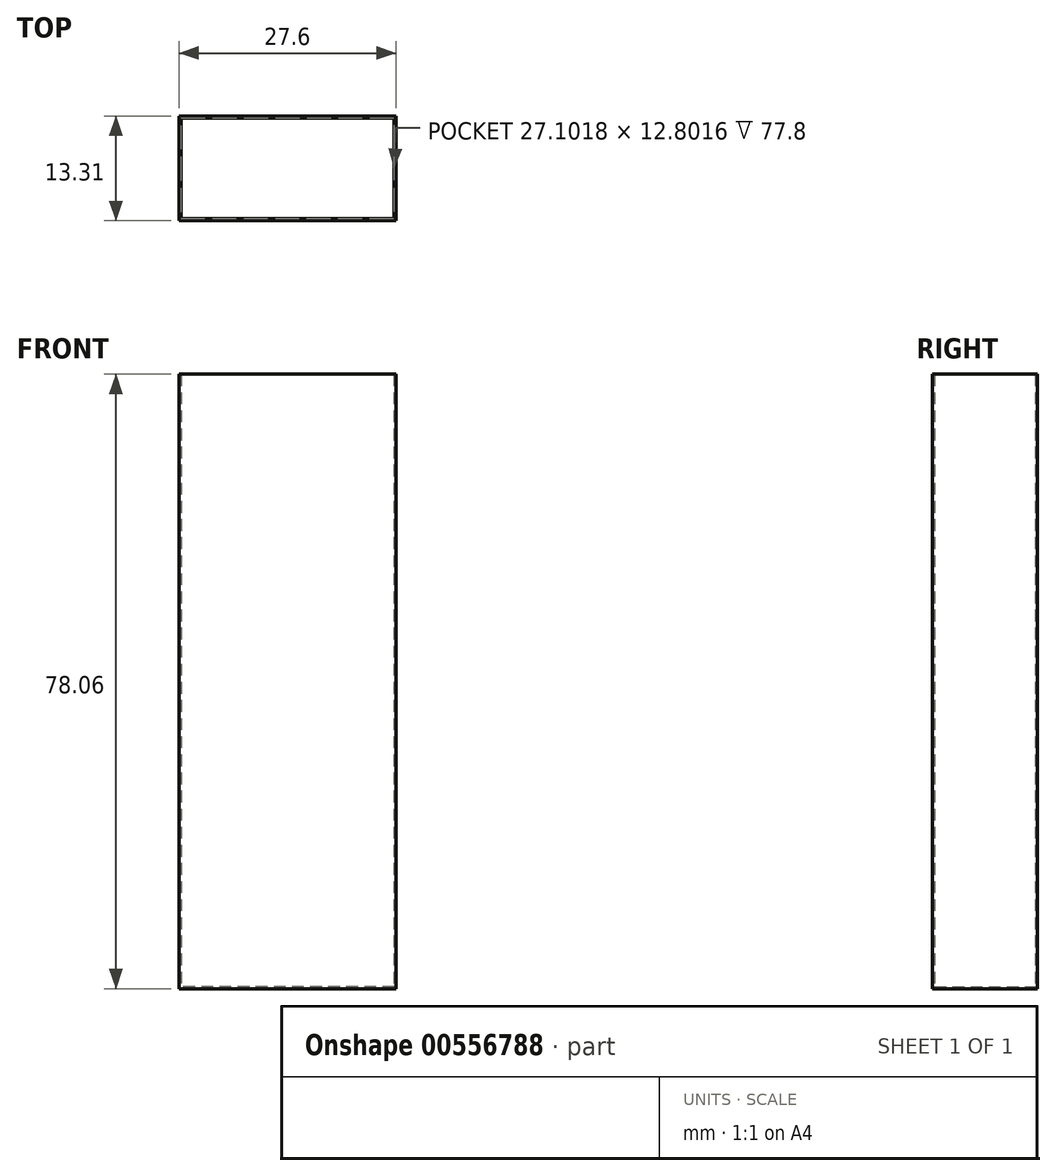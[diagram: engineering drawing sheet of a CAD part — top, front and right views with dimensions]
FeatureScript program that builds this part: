
annotation { "Feature Type Name" : "Feature", "Feature Type Description" : "" }
export const myFeature = defineFeature(function(context is Context, id is Id, definition is map)
    precondition{}
    {
        {
            var Q0;
            Q0=qCreatedBy(makeId("Front.planeOp"),FACE);
            var sketch = newSketch(context, id + "F0", { "sketchPlane" : qUnion([Q0])});
            skLineSegment(sketch, "E0.bottom", {"start": v(13.8, 39.03) * mm, "end": v(-13.8, 39.03) * mm});
            skLineSegment(sketch, "E0.top", {"start": v(13.8, -39.03) * mm, "end": v(-13.8, -39.03) * mm});
            skLineSegment(sketch, "E0.left", {"start": v(13.8, 39.03) * mm, "end": v(13.8, -39.03) * mm});
            skLineSegment(sketch, "E0.right", {"start": v(-13.8, 39.03) * mm, "end": v(-13.8, -39.03) * mm});
            skPoint(sketch, "E0.middle", {"position": v(0, 0) * mm});
            skSolve(sketch);
        }
        {
            var Q0;
            Q0=makeQuery(id+"F0.imprint","IMPRINT",FACE,{"disambiguationData":[TD([[makeQuery(id+"F0.imprint","IMPRINT",EDGE,{"derivedFrom":sQuery(id+"F0.wireOp",EDGE,"E0.bottom")}),1.0]])]});
            extrude(context, id + "F1", {"entities" : qUnion([Q0]), "depth" : 13.3 * mm, "offsetDistance" : 25.4 * mm});
        }
        {
            var Q0;
            Q0=makeQuery(id+"F1.opExtrude","SWEPT_FACE",FACE,{"disambiguationData":[OSD([sQuery(id+"F0.wireOp",EDGE,"E0.bottom")])]});
            var Q1;
            Q1=makeQuery(id+"F1.opExtrude","SWEPT_BODY",BODY,{"disambiguationData":[OSD([sQuery(id+"F0.wireOp",EDGE,"E0.bottom"),sQuery(id+"F0.wireOp",EDGE,"E0.top"),sQuery(id+"F0.wireOp",EDGE,"E0.left"),sQuery(id+"F0.wireOp",EDGE,"E0.right")])]});
            shell(context, id + "F2", {"entities" : qUnion([Q0]), "parts" : qUnion([Q1]), "thickness" : 0.25 * mm});
        }
    });
